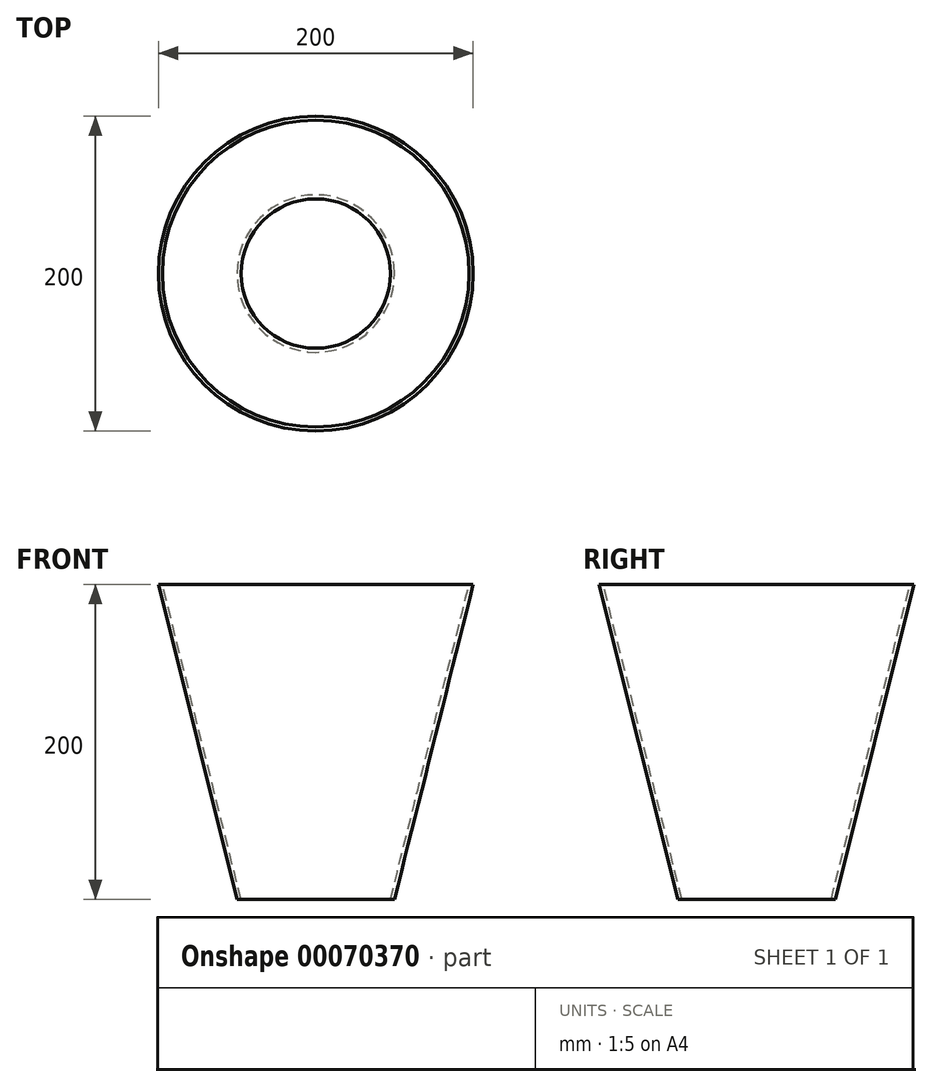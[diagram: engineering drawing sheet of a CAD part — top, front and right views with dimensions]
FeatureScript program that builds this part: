
annotation { "Feature Type Name" : "Feature", "Feature Type Description" : "" }
export const myFeature = defineFeature(function(context is Context, id is Id, definition is map)
    precondition{}
    {
        {
            var Q0;
            Q0=qCreatedBy(makeId("Top.planeOp"),FACE);
            var sketch = newSketch(context, id + "F0", { "sketchPlane" : qUnion([Q0])});
            skCircle(sketch, "E0", {"center": v(0, 0) * mm, "radius": 50 * mm});
            skSolve(sketch);
        }
        {
            var Q0;
            Q0=qCreatedBy(makeId("Top.planeOp"),FACE);
            cPlane(context, id + "F1", {"entities" : qUnion([Q0]), "cplaneType" : CPlaneType.OFFSET, "offset" : 200 * mm, "width" : 150 * mm, "height" : 150 * mm});
        }
        {
            var Q0;
            Q0=qCreatedBy(id+"F1.planeOp",FACE);
            var sketch = newSketch(context, id + "F2", { "sketchPlane" : qUnion([Q0])});
            skCircle(sketch, "E1", {"center": v(0, 0) * mm, "radius": 100 * mm});
            skSolve(sketch);
        }
        {
            var Q0;
            Q0=makeQuery(id+"F0.imprint","IMPRINT",FACE,{"disambiguationData":[TD([[makeQuery(id+"F0.imprint","IMPRINT",EDGE,{"derivedFrom":sQuery(id+"F0.wireOp",EDGE,"E0")}),1.0]])]});
            var Q1;
            Q1=makeQuery(id+"F2.imprint","IMPRINT",FACE,{"disambiguationData":[TD([[makeQuery(id+"F2.imprint","IMPRINT",EDGE,{"derivedFrom":sQuery(id+"F2.wireOp",EDGE,"E1")}),1.0]])]});
            loft(context, id + "F3", {"sheetProfilesArray" : [{ "sheetProfileEntities" : qUnion([Q0]) }, { "sheetProfileEntities" : qUnion([Q1]) }]});
        }
        {
            var Q0;
            Q0=makeQuery(id+"F3.opLoft","CAP_FACE",FACE,{"disambiguationData":[OSD([makeQuery(id+"F2.imprint","IMPRINT",FACE,{"disambiguationData":[TD([[makeQuery(id+"F2.imprint","IMPRINT",EDGE,{"derivedFrom":sQuery(id+"F2.wireOp",EDGE,"E1")}),1.0]])]})])],"isStart":true});
            var Q1;
            Q1=makeQuery(id+"F3.opLoft","CAP_FACE",FACE,{"disambiguationData":[OSD([makeQuery(id+"F0.imprint","IMPRINT",FACE,{"disambiguationData":[TD([[makeQuery(id+"F0.imprint","IMPRINT",EDGE,{"derivedFrom":sQuery(id+"F0.wireOp",EDGE,"E0")}),1.0]])]})])],"isStart":true});
            shell(context, id + "F4", {"entities" : qUnion([Q0, Q1]), "thickness" : 2.5 * mm});
        }
    });
